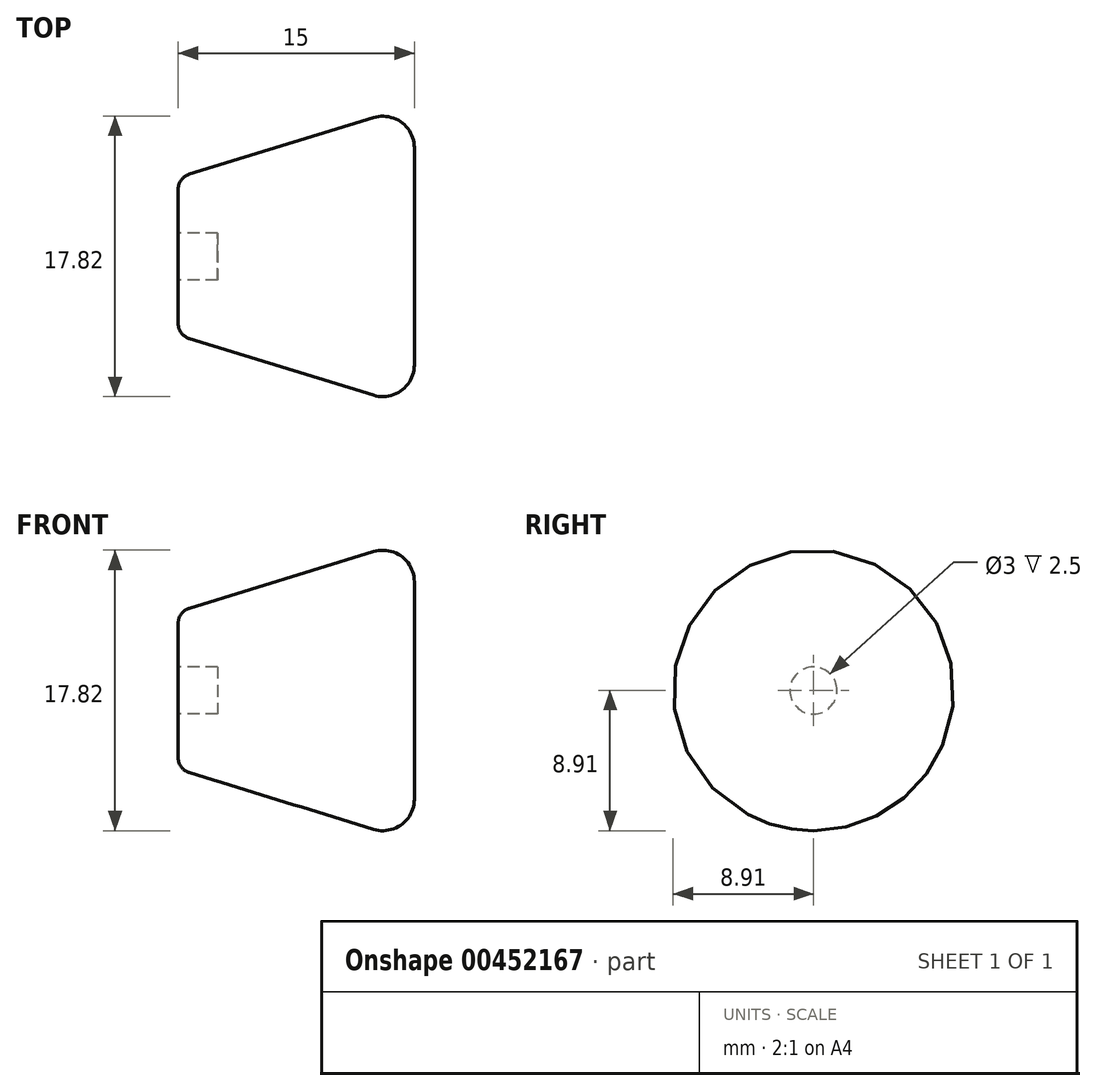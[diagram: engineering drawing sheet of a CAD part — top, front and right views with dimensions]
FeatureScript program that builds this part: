
annotation { "Feature Type Name" : "Feature", "Feature Type Description" : "" }
export const myFeature = defineFeature(function(context is Context, id is Id, definition is map)
    precondition{}
    {
        {
            var Q0;
            Q0=qCreatedBy(makeId("Right.planeOp"),FACE);
            var sketch = newSketch(context, id + "F0", { "sketchPlane" : qUnion([Q0])});
            skCircle(sketch, "E0", {"center": v(0, 0) * mm, "radius": 5 * mm});
            skSolve(sketch);
        }
        {
            var Q0;
            Q0 = qSketchRegion(id + "F0", true);
            extrude(context, id + "F1", {"entities" : qUnion([Q0]), "depth" : 15 * mm, "hasDraft" : true, "draftAngle" : 17.1 * degree});
        }
        {
            var Q0;
            Q0=makeQuery(id+"F1.opExtrude","CAP_EDGE",EDGE,{"disambiguationData":[OSD([sQuery(id+"F0.wireOp",EDGE,"E0")])],"isStart":false});
            fillet(context, id + "F2", {"entities" : qUnion([Q0]), "radius" : 2 * mm, "tangentPropagation" : true, "allowEdgeOverflow" : false});
        }
        {
            var Q0;
            Q0=makeQuery(id+"F1.opExtrude","CAP_EDGE",EDGE,{"disambiguationData":[OSD([sQuery(id+"F0.wireOp",EDGE,"E0")])],"isStart":true});
            fillet(context, id + "F3", {"entities" : qUnion([Q0]), "radius" : 1 * mm, "tangentPropagation" : true, "allowEdgeOverflow" : false});
        }
        {
            var Q0;
            Q0=makeQuery(id+"F1.opExtrude","CAP_FACE",FACE,{"disambiguationData":[OSD([sQuery(id+"F0.wireOp",EDGE,"E0")])],"isStart":true});
            var sketch = newSketch(context, id + "F4", { "sketchPlane" : qUnion([Q0])});
            skCircle(sketch, "E1", {"center": v(0, 0) * mm, "radius": 1.5 * mm});
            skSolve(sketch);
        }
        {
            var Q0;
            Q0=makeQuery(id+"F4.imprint","IMPRINT",FACE,{"disambiguationData":[TD([[makeQuery(id+"F4.imprint","IMPRINT",EDGE,{"derivedFrom":sQuery(id+"F4.wireOp",EDGE,"E1")}),1.0]])]});
            var Q1;
            Q1=sQuery(id+"F4.wireOp",EDGE,"E1");
            extrude(context, id + "F5", {"entities" : qUnion([Q0]), "operationType" : NewBodyOperationType.REMOVE, "surfaceEntities" : qUnion([Q1]), "oppositeDirection" : true, "depth" : 2.5 * mm});
        }
    });
